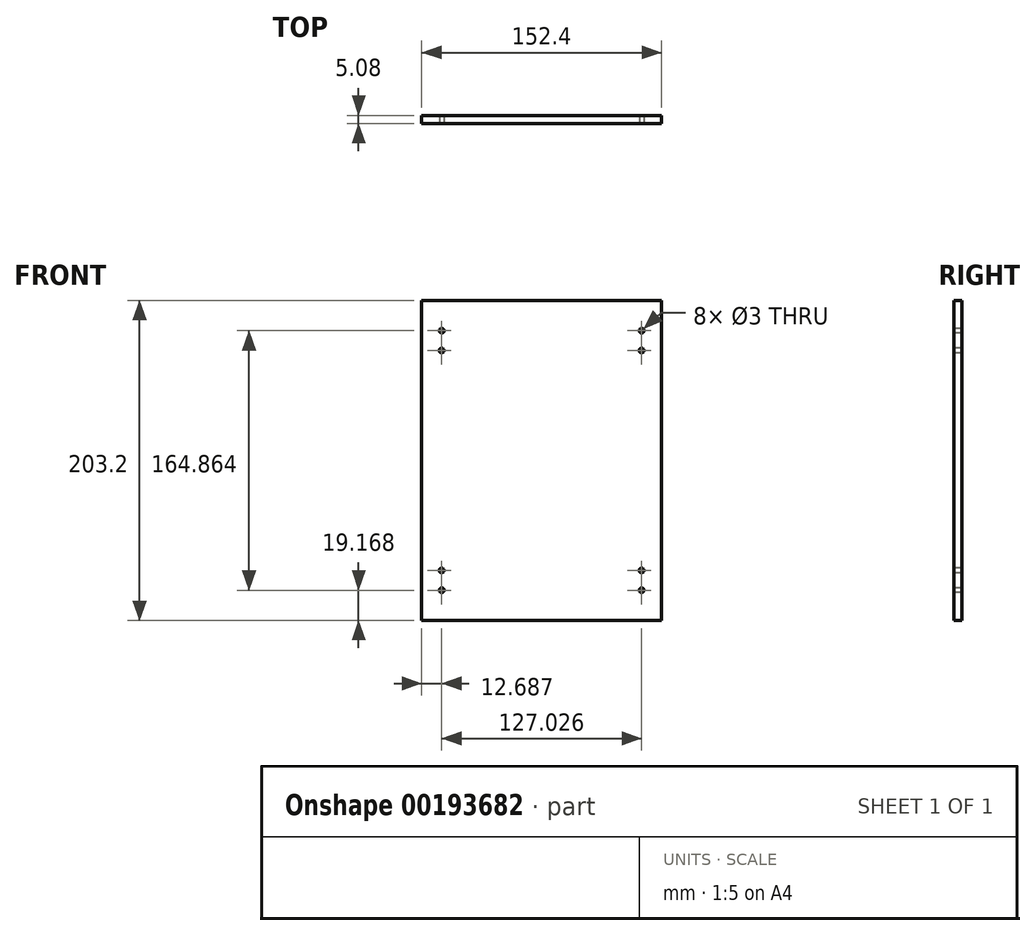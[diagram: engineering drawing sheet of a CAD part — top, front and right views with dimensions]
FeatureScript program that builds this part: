
annotation { "Feature Type Name" : "Feature", "Feature Type Description" : "" }
export const myFeature = defineFeature(function(context is Context, id is Id, definition is map)
    precondition{}
    {
        {
            var Q0;
            Q0=qCreatedBy(makeId("Front.planeOp"),FACE);
            var sketch = newSketch(context, id + "F0", { "sketchPlane" : qUnion([Q0])});
            skLineSegment(sketch, "E0.bottom", {"start": v(-76.2, 101.6) * mm, "end": v(76.2, 101.6) * mm});
            skLineSegment(sketch, "E0.top", {"start": v(-76.2, -101.6) * mm, "end": v(76.2, -101.6) * mm});
            skLineSegment(sketch, "E0.left", {"start": v(-76.2, 101.6) * mm, "end": v(-76.2, -101.6) * mm});
            skLineSegment(sketch, "E0.right", {"start": v(76.2, 101.6) * mm, "end": v(76.2, -101.6) * mm});
            skPoint(sketch, "E0.middle", {"position": v(0, 0) * mm});
            skSolve(sketch);
        }
        {
            var Q0;
            Q0=makeQuery(id+"F0.imprint","IMPRINT",FACE,{"disambiguationData":[TD([[makeQuery(id+"F0.imprint","IMPRINT",EDGE,{"derivedFrom":sQuery(id+"F0.wireOp",EDGE,"E0.bottom")}),-1.0]])]});
            extrude(context, id + "F1", {"entities" : qUnion([Q0]), "depth" : 5.08 * mm});
        }
        {
            var Q0;
            Q0=makeQuery(id+"F1.opExtrude","CAP_FACE",FACE,{"disambiguationData":[OSD([sQuery(id+"F0.wireOp",EDGE,"E0.bottom"),sQuery(id+"F0.wireOp",EDGE,"E0.top"),sQuery(id+"F0.wireOp",EDGE,"E0.left"),sQuery(id+"F0.wireOp",EDGE,"E0.right")])],"isStart":false});
            var sketch = newSketch(context, id + "F2", { "sketchPlane" : qUnion([Q0])});
            skLineSegment(sketch, "E1", {"start": v(-63.5, 101.6) * mm, "end": v(-63.5, 82.55) * mm});
            skLineSegment(sketch, "E2", {"start": v(-63.5, 82.55) * mm, "end": v(-63.5, 69.85) * mm});
            skSolve(sketch);
        }
        {
            var Q0;
            Q0=makeQuery(id+"F2.imprint","IMPRINT",FACE,{"disambiguationData":[TD([[makeQuery(id+"F2.imprint","IMPRINT",EDGE,{"derivedFrom":makeQuery(id+"F1.opExtrude","CAP_EDGE",EDGE,{"disambiguationData":[OSD([sQuery(id+"F0.wireOp",EDGE,"E0.top")])],"isStart":false})}),1.0]])]});
            var sketch = newSketch(context, id + "F3", { "sketchPlane" : qUnion([Q0])});
            skCircle(sketch, "E3", {"center": v(-63.48, 82.43) * mm, "radius": 1.5 * mm});
            skCircle(sketch, "E4", {"center": v(-63.51, 69.86) * mm, "radius": 1.5 * mm});
            skSolve(sketch);
        }
        {
            var Q0;
            Q0 = qSketchRegion(id + "F3", true);
            extrude(context, id + "F4", {"entities" : qUnion([Q0]), "operationType" : NewBodyOperationType.REMOVE, "oppositeDirection" : true, "depth" : .3 * mm});
        }
        {
            var Q0;
            Q0 = qSketchRegion(id + "F3", true);
            extrude(context, id + "F5", {"entities" : qUnion([Q0]), "operationType" : NewBodyOperationType.REMOVE, "oppositeDirection" : true, "depth" : 25.4 * mm});
        }
        {
            var Q0;
            Q0=makeQuery(id+"F1.opExtrude","SWEPT_BODY",BODY,{"disambiguationData":[OSD([sQuery(id+"F0.wireOp",EDGE,"E0.bottom"),sQuery(id+"F0.wireOp",EDGE,"E0.top"),sQuery(id+"F0.wireOp",EDGE,"E0.left"),sQuery(id+"F0.wireOp",EDGE,"E0.right")])]});
            var Q1;
            Q1=qCreatedBy(makeId("Right.planeOp"),FACE);
            mirror(context, id + "F6", {"operationType" : NewBodyOperationType.INTERSECT, "entities" : qUnion([Q0]), "mirrorPlane" : qUnion([Q1])});
        }
        {
            var Q0;
            Q0=makeQuery(id+"F1.opExtrude","SWEPT_BODY",BODY,{"disambiguationData":[OSD([sQuery(id+"F0.wireOp",EDGE,"E0.bottom"),sQuery(id+"F0.wireOp",EDGE,"E0.top"),sQuery(id+"F0.wireOp",EDGE,"E0.left"),sQuery(id+"F0.wireOp",EDGE,"E0.right")])]});
            var Q1;
            Q1=qCreatedBy(makeId("Top.planeOp"),FACE);
            mirror(context, id + "F7", {"operationType" : NewBodyOperationType.INTERSECT, "entities" : qUnion([Q0]), "mirrorPlane" : qUnion([Q1])});
        }
    });
